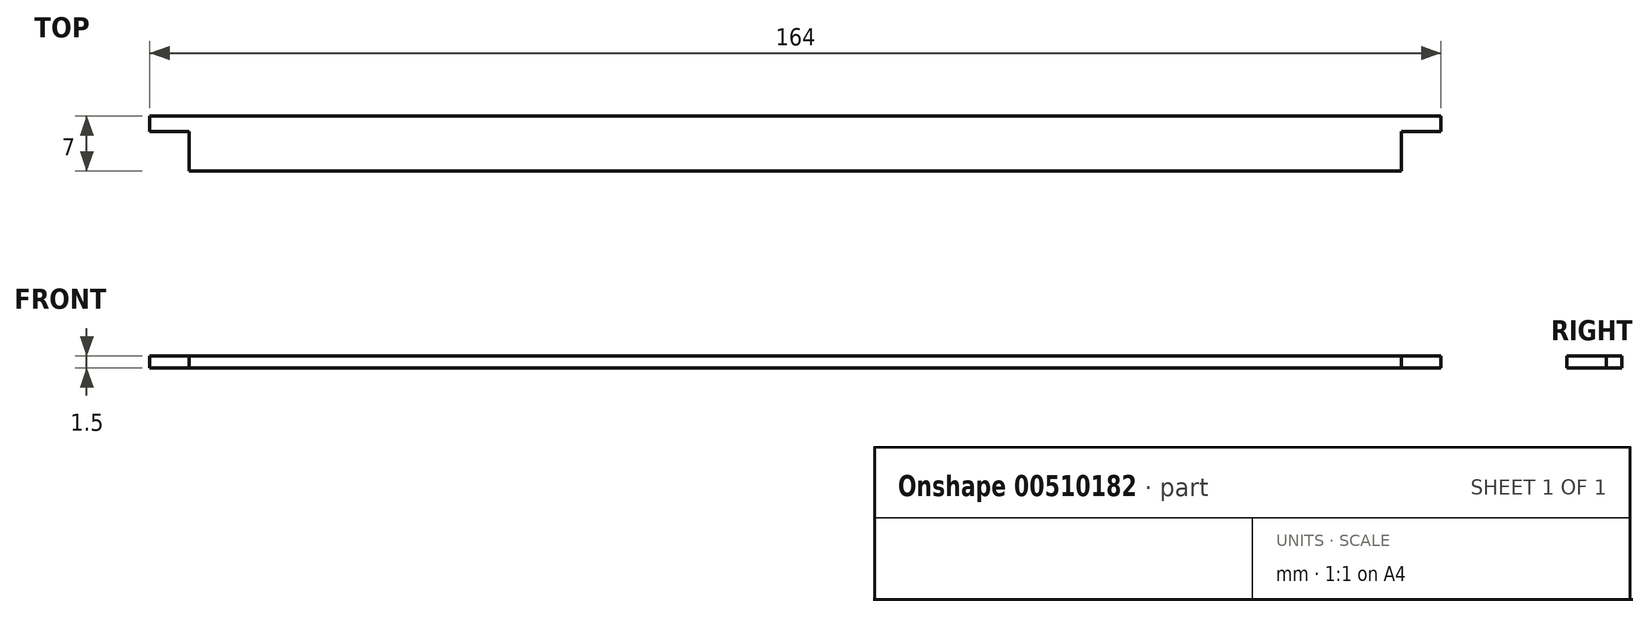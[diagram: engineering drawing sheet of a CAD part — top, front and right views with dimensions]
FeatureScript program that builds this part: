
annotation { "Feature Type Name" : "Feature", "Feature Type Description" : "" }
export const myFeature = defineFeature(function(context is Context, id is Id, definition is map)
    precondition{}
    {
        {
            var Q0;
            Q0=qCreatedBy(makeId("Top.planeOp"),FACE);
            var sketch = newSketch(context, id + "F0", { "sketchPlane" : qUnion([Q0])});
            skLineSegment(sketch, "E0", {"start": v(-79.28, 0) * mm, "end": v(84.72, 0) * mm});
            skLineSegment(sketch, "E1", {"start": v(84.72, 0) * mm, "end": v(84.72, -2) * mm});
            skLineSegment(sketch, "E2", {"start": v(84.72, -2) * mm, "end": v(79.72, -2) * mm});
            skLineSegment(sketch, "E3", {"start": v(79.72, -2) * mm, "end": v(79.72, -7) * mm});
            skLineSegment(sketch, "E4", {"start": v(79.72, -7) * mm, "end": v(-74.28, -7) * mm});
            skLineSegment(sketch, "E5", {"start": v(-74.28, -7) * mm, "end": v(-74.28, -2) * mm});
            skLineSegment(sketch, "E6", {"start": v(-74.28, -2) * mm, "end": v(-79.28, -2) * mm});
            skLineSegment(sketch, "E7", {"start": v(-79.28, -2) * mm, "end": v(-79.28, 0) * mm});
            skSolve(sketch);
        }
        {
            var Q0;
            Q0 = qSketchRegion(id + "F0", true);
            extrude(context, id + "F1", {"entities" : qUnion([Q0]), "depth" : 1.5 * mm});
        }
    });
